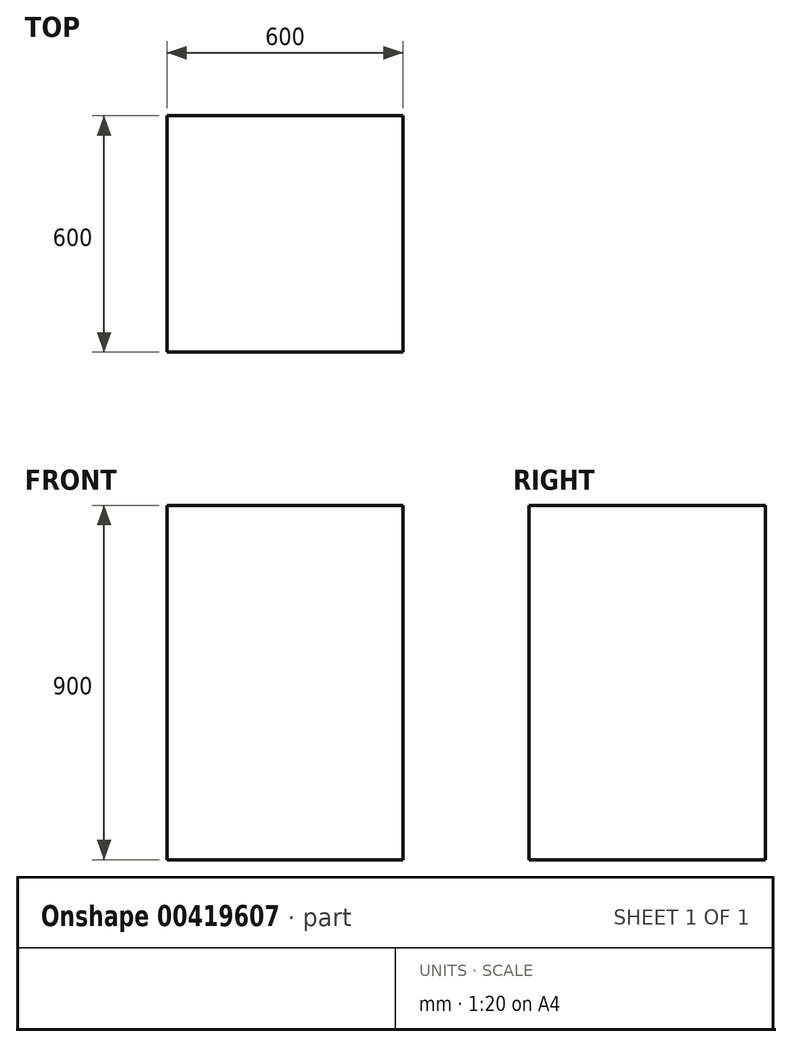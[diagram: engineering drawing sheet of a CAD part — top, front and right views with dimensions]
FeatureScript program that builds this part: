
annotation { "Feature Type Name" : "Feature", "Feature Type Description" : "" }
export const myFeature = defineFeature(function(context is Context, id is Id, definition is map)
    precondition{}
    {
        {
            var Q0;
            Q0=qCreatedBy(makeId("Top.planeOp"),FACE);
            var sketch = newSketch(context, id + "F0", { "sketchPlane" : qUnion([Q0])});
            skLineSegment(sketch, "E0.bottom", {"start": v(-537.9, 538.62) * mm, "end": v(62.1, 538.62) * mm});
            skLineSegment(sketch, "E0.top", {"start": v(-537.9, -61.38) * mm, "end": v(62.1, -61.38) * mm});
            skLineSegment(sketch, "E0.left", {"start": v(-537.9, 538.62) * mm, "end": v(-537.9, -61.38) * mm});
            skLineSegment(sketch, "E0.right", {"start": v(62.1, 538.62) * mm, "end": v(62.1, -61.38) * mm});
            skSolve(sketch);
        }
        {
            var Q0;
            Q0=makeQuery(id+"F0.imprint","IMPRINT",FACE,{"disambiguationData":[TD([[makeQuery(id+"F0.imprint","IMPRINT",EDGE,{"derivedFrom":sQuery(id+"F0.wireOp",EDGE,"E0.bottom")}),-1.0]])]});
            extrude(context, id + "F1", {"entities" : qUnion([Q0]), "depth" : 900 * mm});
        }
    });
